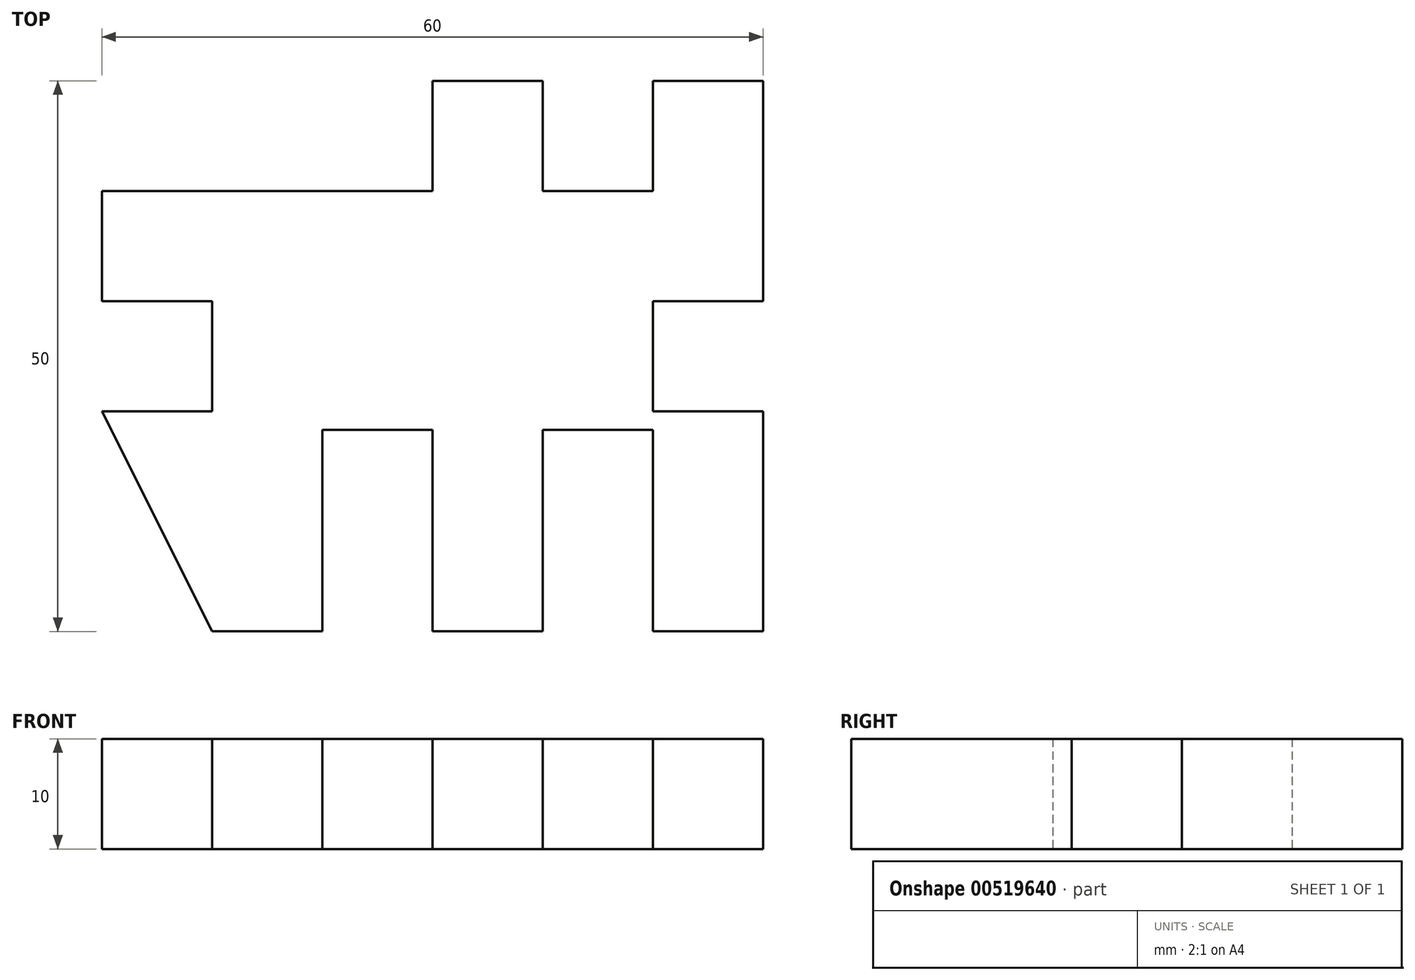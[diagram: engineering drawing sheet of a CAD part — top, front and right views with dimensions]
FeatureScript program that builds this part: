
annotation { "Feature Type Name" : "Feature", "Feature Type Description" : "" }
export const myFeature = defineFeature(function(context is Context, id is Id, definition is map)
    precondition{}
    {
        {
            var Q0;
            Q0=qCreatedBy(makeId("Top.planeOp"),FACE);
            var sketch = newSketch(context, id + "F0", { "sketchPlane" : qUnion([Q0])});
            skLineSegment(sketch, "E0", {"start": v(-29.91, 29.48) * mm, "end": v(-10, 29.48) * mm});
            skLineSegment(sketch, "E1", {"start": v(-10, 39.48) * mm, "end": v(-10, 29.48) * mm});
            skLineSegment(sketch, "E2", {"start": v(0, 39.48) * mm, "end": v(-10, 39.48) * mm});
            skLineSegment(sketch, "E3", {"start": v(0, 29.48) * mm, "end": v(10, 29.48) * mm});
            skLineSegment(sketch, "E4", {"start": v(10, 29.48) * mm, "end": v(10, 39.48) * mm});
            skLineSegment(sketch, "E5", {"start": v(10, 39.48) * mm, "end": v(20, 39.48) * mm});
            skLineSegment(sketch, "E6", {"start": v(20, 39.48) * mm, "end": v(20, 19.48) * mm});
            skLineSegment(sketch, "E7", {"start": v(20, 19.48) * mm, "end": v(10, 19.48) * mm});
            skLineSegment(sketch, "E8", {"start": v(10, 19.48) * mm, "end": v(10, 9.48) * mm});
            skLineSegment(sketch, "E9", {"start": v(10, 9.48) * mm, "end": v(20, 9.48) * mm});
            skLineSegment(sketch, "E10", {"start": v(20, 9.48) * mm, "end": v(20, -10.52) * mm});
            skLineSegment(sketch, "E11", {"start": v(20, -10.52) * mm, "end": v(10, -10.52) * mm});
            skLineSegment(sketch, "E12", {"start": v(10, -10.52) * mm, "end": v(10, 7.78) * mm});
            skLineSegment(sketch, "E13", {"start": v(10, 7.78) * mm, "end": v(0, 7.78) * mm});
            skLineSegment(sketch, "E14", {"start": v(0, 7.78) * mm, "end": v(0, -10.52) * mm});
            skLineSegment(sketch, "E15", {"start": v(0, -10.52) * mm, "end": v(-10, -10.52) * mm});
            skLineSegment(sketch, "E16", {"start": v(-10, -10.52) * mm, "end": v(-10, 7.78) * mm});
            skLineSegment(sketch, "E17", {"start": v(-10, 7.78) * mm, "end": v(-20, 7.78) * mm});
            skLineSegment(sketch, "E18", {"start": v(-20, 7.78) * mm, "end": v(-20, -10.52) * mm});
            skLineSegment(sketch, "E19", {"start": v(-20, -10.52) * mm, "end": v(-30, -10.52) * mm});
            skLineSegment(sketch, "E20", {"start": v(-40, 9.48) * mm, "end": v(-30, 9.48) * mm});
            skLineSegment(sketch, "E21", {"start": v(-30, 9.48) * mm, "end": v(-30, 19.48) * mm});
            skLineSegment(sketch, "E22", {"start": v(-30, 19.48) * mm, "end": v(-40, 19.48) * mm});
            skLineSegment(sketch, "E23", {"start": v(-40, 19.48) * mm, "end": v(-40, 29.48) * mm});
            skLineSegment(sketch, "E24", {"start": v(-40, 29.48) * mm, "end": v(-29.91, 29.48) * mm});
            skLineSegment(sketch, "E25", {"start": v(0, 39.48) * mm, "end": v(0, 29.48) * mm});
            skLineSegment(sketch, "E26", {"start": v(-40, 9.48) * mm, "end": v(-30, -10.52) * mm});
            skSolve(sketch);
        }
        {
            var Q0;
            Q0=makeQuery(id+"F0.imprint","IMPRINT",FACE,{"disambiguationData":[TD([[makeQuery(id+"F0.imprint","IMPRINT",EDGE,{"derivedFrom":sQuery(id+"F0.wireOp",EDGE,"E0")}),-1.0]])]});
            extrude(context, id + "F1", {"entities" : qUnion([Q0]), "depth" : 10 * mm, "offsetDistance" : 25 * mm});
        }
    });
